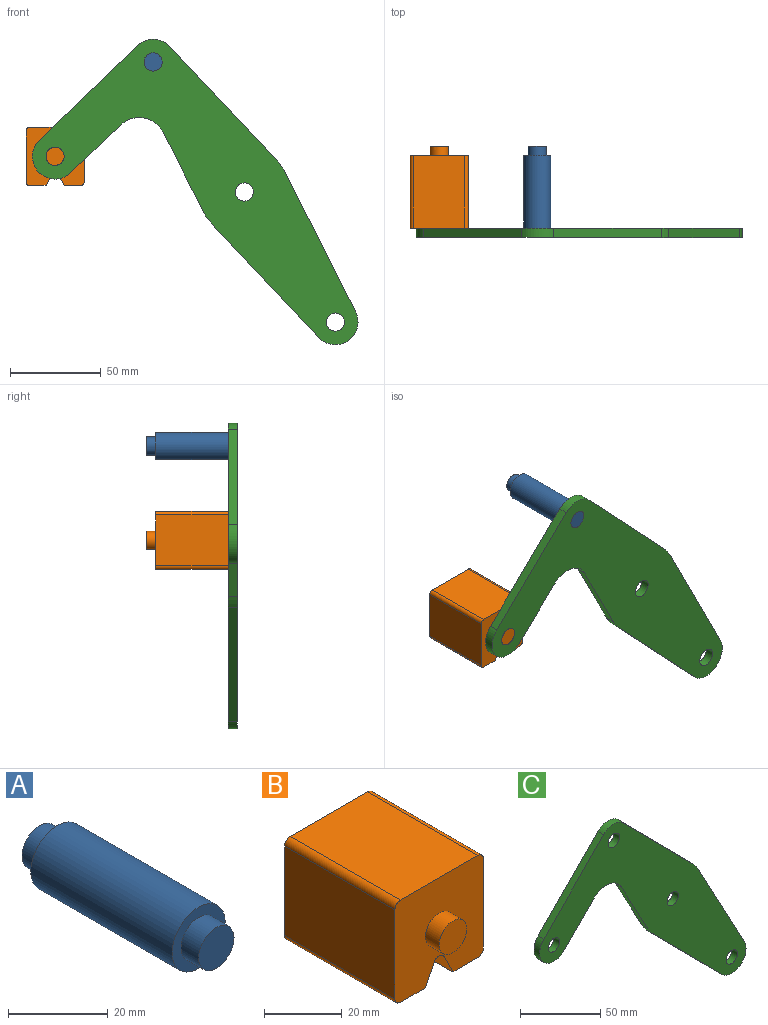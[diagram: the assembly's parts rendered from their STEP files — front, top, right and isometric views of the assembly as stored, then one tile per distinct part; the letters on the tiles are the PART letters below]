
ASSEMBLY  parts=3 mates=1
PART A: 7 faces, bbox 15x50x15 mm
  f0: cylinder r=7.5mm len=40mm, axis (0,-1,0), area 1885mm2, adj f2,f5
  f1: cylinder r=5mm len=10mm, axis (0,1,0), area 157.1mm2, adj f2,f3
  f2: plane 15x15mm, normal (0,-1,0), area 98.2mm2, adj f0,f1
  f3: plane 10x10mm, normal (0,-1,0), area 78.5mm2, adj f1
  f4: cylinder r=5mm len=10mm, axis (0,-1,0), area 157.1mm2, adj f5,f6
  f5: plane 15x15mm, normal (0,1,0), area 98.2mm2, adj f0,f4
  f6: plane 10x10mm, normal (0,1,0), area 78.5mm2, adj f4
PART B: 18 faces, bbox 32.1x50x32.1 mm
  f0: plane 40x28.08mm, normal (1,0,0), area 1123.1mm2, adj f4,f10,f13,f14
  f1: plane 40x9.04mm, normal (0,0,-1), area 361.6mm2, adj f2,f4,f10,f14
  f2: plane 40x6.42mm, normal (-0.89,0,-0.45), area 287.2mm2, adj f1,f4,f10,f15
  f3: plane 40x6.42mm, normal (0.89,0,-0.45), area 287.2mm2, adj f4,f5,f10,f15
  f4: plane 32.08x32.08mm, normal (0,-1,0), area 900.6mm2, adj f0,f1,f2,f3,f5,f6,f7,f9
  f5: plane 40x9.04mm, normal (0,0,-1), area 361.6mm2, adj f3,f4,f10,f16
  f6: plane 40x28.08mm, normal (0,0,1), area 1123.1mm2, adj f4,f10,f13,f17
  f7: plane 40x28.08mm, normal (-1,0,0), area 1123.1mm2, adj f4,f10,f16,f17
  f8: plane 10x10mm, normal (0,-1,0), area 78.5mm2, adj f9
  f9: cylinder r=5mm len=10mm, axis (0,1,0), area 157.1mm2, adj f4,f8
  f10: plane 32.08x32.08mm, normal (0,1,0), area 900.6mm2, adj f0,f1,f2,f3,f5,f6,f7,f12
  f11: plane 10x10mm, normal (0,1,0), area 78.5mm2, adj f12
  f12: cylinder r=5mm len=10mm, axis (0,-1,0), area 157.1mm2, adj f10,f11
  f13: cylinder r=2mm len=40mm, axis (0,1,0), area 125.7mm2, adj f0,f4,f6,f10
  f14: cylinder r=2mm len=40mm, axis (0,-1,0), area 125.7mm2, adj f0,f1,f4,f10
  f15: cylinder r=2mm len=40mm, axis (0,1,0), area 177.1mm2, adj f2,f3,f4,f10
  f16: cylinder r=2mm len=40mm, axis (0,1,0), area 125.7mm2, adj f4,f5,f7,f10
  f17: cylinder r=2mm len=40mm, axis (0,-1,0), area 125.7mm2, adj f4,f6,f7,f10
PART C: 18 faces, bbox 181.7x5x165.8 mm
  f0: plane 43.49x23.35mm, normal (-0.88,0,-0.47), area 246.8mm2, adj f1,f14,f16,f17
  f1: cylinder r=25mm len=5.75mm, axis (0,1,0), area 35.8mm2, adj f0,f2,f16,f17
  f2: plane 61.6x60.87mm, normal (-0.71,0,-0.7), area 433mm2, adj f1,f3,f16,f17
  f3: cylinder r=12.5mm len=21.39mm, axis (0,1,0), area 178.4mm2, adj f2,f4,f16,f17
  f4: plane 76.3x40.96mm, normal (0.88,0,0.47), area 433mm2, adj f3,f5,f16,f17
  f5: cylinder r=25mm len=5.75mm, axis (0,1,0), area 35.8mm2, adj f4,f6,f16,f17
  f6: plane 61.6x60.87mm, normal (0.71,0,0.7), area 433mm2, adj f5,f7,f16,f17
  f7: cylinder r=12.5mm len=17.78mm, axis (0,1,0), area 98.9mm2, adj f6,f8,f16,f17
  f8: plane 53.35x52.71mm, normal (-0.71,0,0.7), area 375mm2, adj f7,f9,f16,f17
  f9: cylinder r=12.5mm len=21.39mm, axis (0,1,0), area 196.3mm2, adj f8,f10,f16,f17
  f10: plane 26.86x26.54mm, normal (0.71,0,-0.7), area 188.8mm2, adj f9,f14,f16,f17
  f11: cylinder r=5mm len=10mm, axis (0,1,0), area 157.1mm2, adj f16,f17
  f12: cylinder r=5mm len=10mm, axis (0,1,0), area 157.1mm2, adj f16,f17
  f13: cylinder r=5mm len=10mm, axis (0,1,0), area 157.1mm2, adj f16,f17
  f14: cylinder r=15mm len=23.89mm, axis (0,1,0), area 140.2mm2, adj f0,f10,f16,f17
  f15: cylinder r=5mm len=10mm, axis (0,1,0), area 157.1mm2, adj f16,f17
  f16: plane 181.66x165.78mm, normal (0,-1,0), area 8710.1mm2, adj f0,f1,f2,f3,f4,f5,f6,f7
  f17: plane 181.66x165.78mm, normal (0,1,0), area 8710.1mm2, adj f0,f1,f2,f3,f4,f5,f6,f7
PLACE A rot(axis=(0,1,0),1.4deg) t=(0,-20,0)mm
PLACE B t=(0.46,-20,2.6)mm
PLACE C rot(axis=(0,1,0),1.4deg) t=(0,-20,0)mm fixed
MATE revolute B.f9 <-> C.f9  axis (0,-1,0) through (-104.23,-20,19.64)mm
